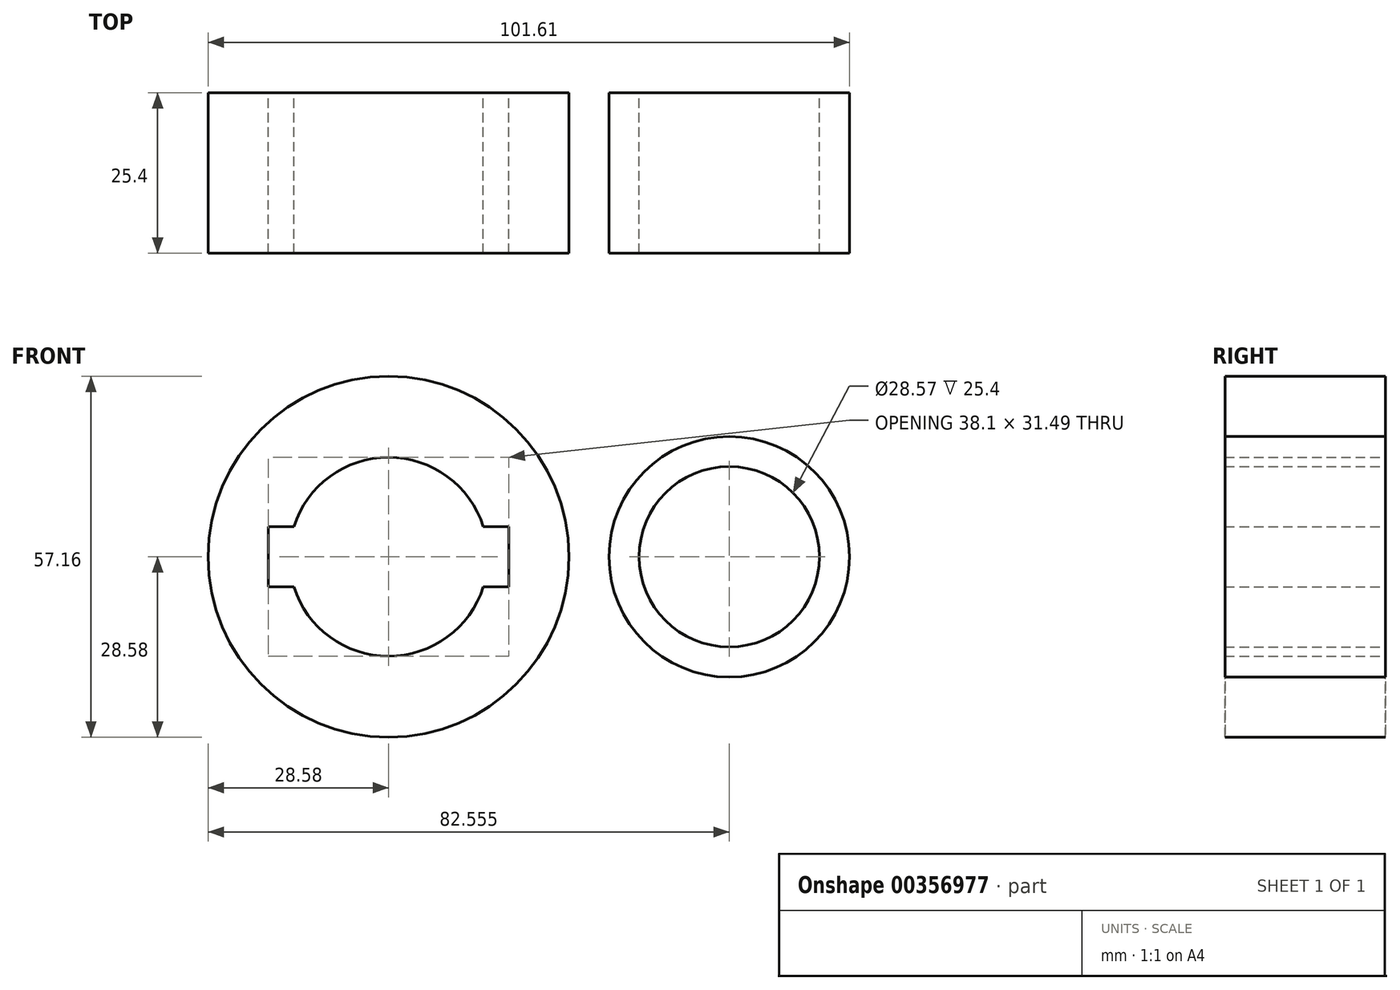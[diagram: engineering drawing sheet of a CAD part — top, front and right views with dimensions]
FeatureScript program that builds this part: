
annotation { "Feature Type Name" : "Feature", "Feature Type Description" : "" }
export const myFeature = defineFeature(function(context is Context, id is Id, definition is map)
    precondition{}
    {
        {
            var Q0;
            Q0=qCreatedBy(makeId("Front.planeOp"),FACE);
            var sketch = newSketch(context, id + "F0", { "sketchPlane" : qUnion([Q0])});
            skCircle(sketch, "E0", {"center": v(0, 0) * mm, "radius": 28.58 * mm});
            skCircle(sketch, "E1", {"center": v(53.97, 0) * mm, "radius": 19.05 * mm});
            skLineSegment(sketch, "E2", {"start": v(3.81, 28.32) * mm, "end": v(57.02, 18.8) * mm});
            skLineSegment(sketch, "E3", {"start": v(3.45, -28.37) * mm, "end": v(57.02, -18.8) * mm});
            skCircle(sketch, "E4", {"center": v(0, 0) * mm, "radius": 15.75 * mm});
            skCircle(sketch, "E5", {"center": v(53.97, 0) * mm, "radius": 14.29 * mm});
            skLineSegment(sketch, "E6.bottom", {"start": v(19.05, 4.76) * mm, "end": v(-19.05, 4.76) * mm});
            skLineSegment(sketch, "E6.top", {"start": v(19.05, -4.76) * mm, "end": v(-19.05, -4.76) * mm});
            skLineSegment(sketch, "E6.left", {"start": v(19.05, 4.76) * mm, "end": v(19.05, -4.76) * mm});
            skLineSegment(sketch, "E6.right", {"start": v(-19.05, 4.76) * mm, "end": v(-19.05, -4.76) * mm});
            skSolve(sketch);
        }
        {
            var Q0;
            Q0 = qSketchRegion(id + "F0", true);
            extrude(context, id + "F1", {"entities" : qUnion([Q0]), "depth" : 25.4 * mm});
        }
    });
